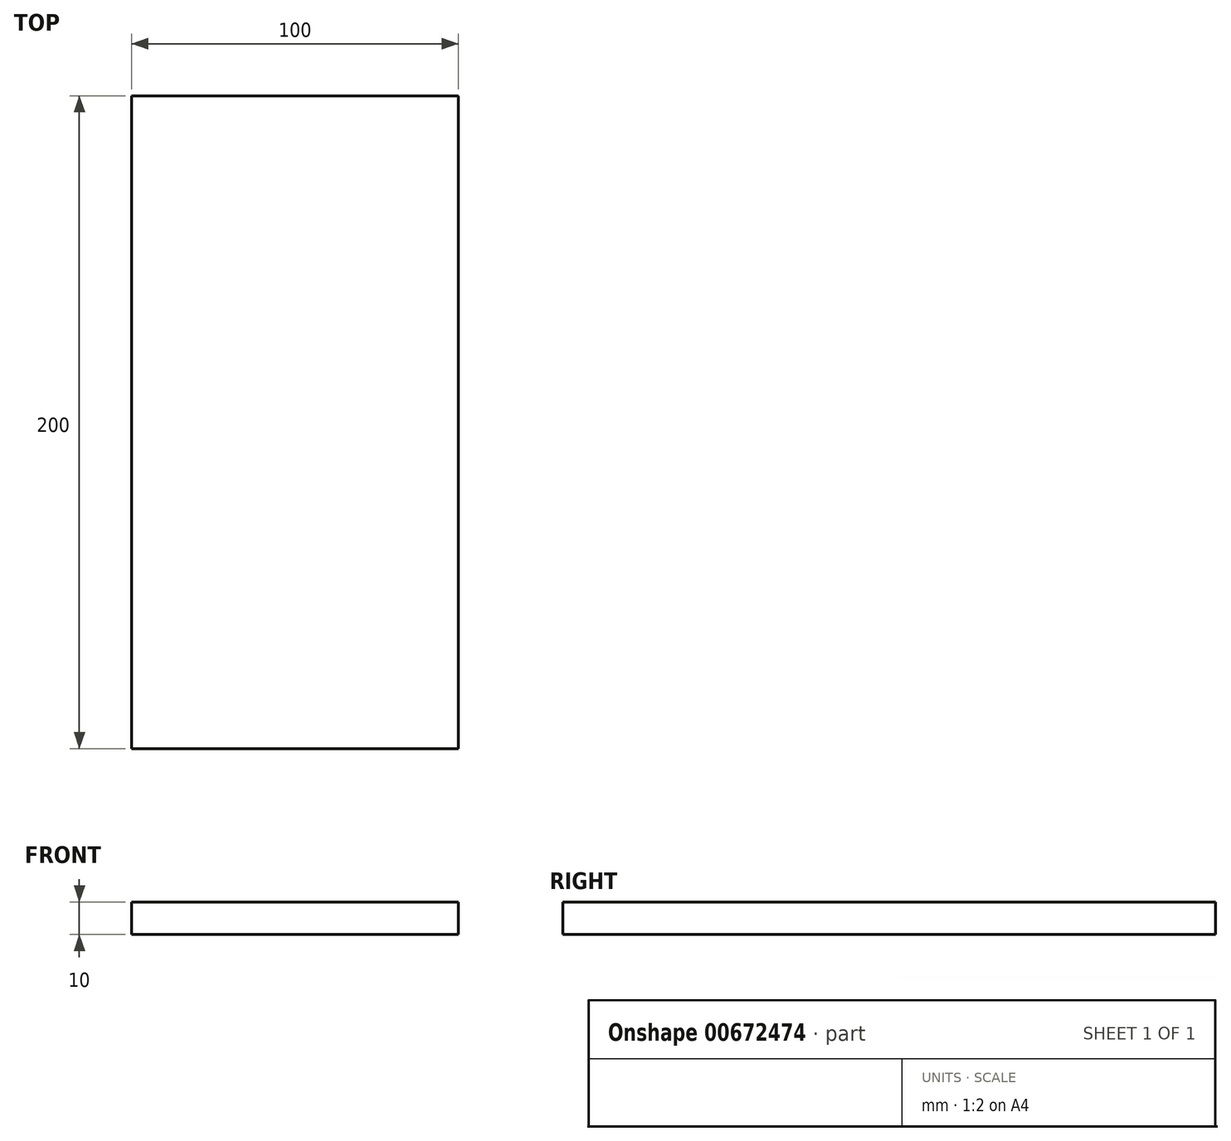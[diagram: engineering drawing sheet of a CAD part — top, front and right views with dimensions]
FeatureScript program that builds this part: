
annotation { "Feature Type Name" : "Feature", "Feature Type Description" : "" }
export const myFeature = defineFeature(function(context is Context, id is Id, definition is map)
    precondition{}
    {
        {
            var Q0;
            Q0=qCreatedBy(makeId("Top.planeOp"),FACE);
            var sketch = newSketch(context, id + "F0", { "sketchPlane" : qUnion([Q0])});
            skLineSegment(sketch, "E0.bottom", {"start": v(50, -100) * mm, "end": v(-50, -100) * mm});
            skLineSegment(sketch, "E0.top", {"start": v(50, 100) * mm, "end": v(-50, 100) * mm});
            skLineSegment(sketch, "E0.left", {"start": v(50, -100) * mm, "end": v(50, 100) * mm});
            skLineSegment(sketch, "E0.right", {"start": v(-50, -100) * mm, "end": v(-50, 100) * mm});
            skPoint(sketch, "E0.middle", {"position": v(0, 0) * mm});
            skSolve(sketch);
        }
        {
            var Q0;
            Q0=qSketchRegion(id+"F0",true);
            extrude(context, id + "F1", {"entities" : qUnion([Q0]), "depth" : 10 * mm, "offsetDistance" : 25 * mm});
        }
    });
